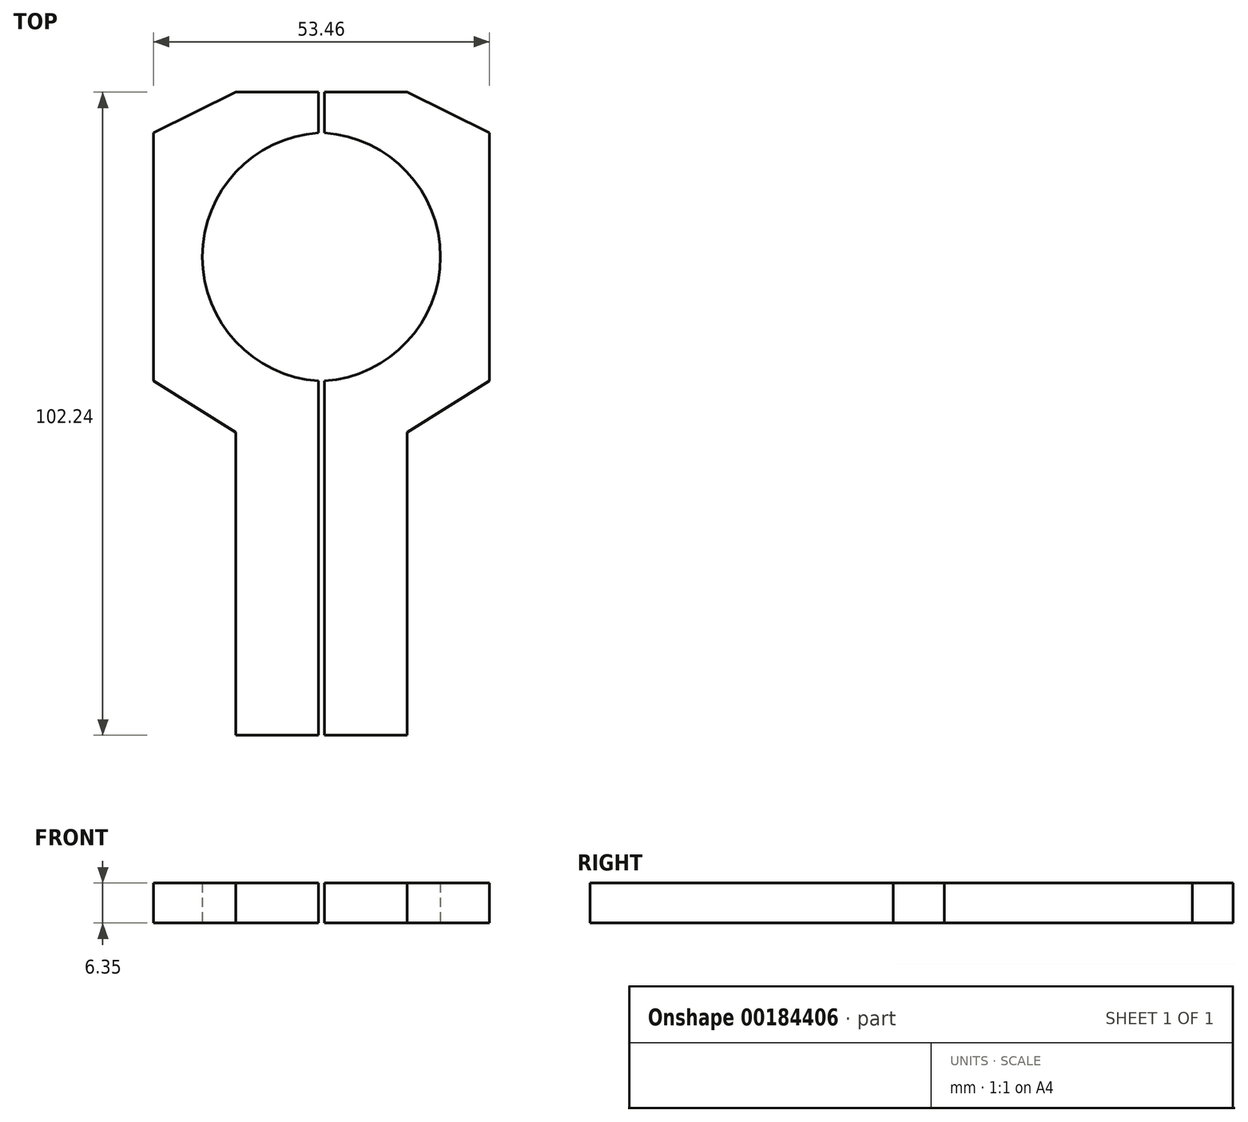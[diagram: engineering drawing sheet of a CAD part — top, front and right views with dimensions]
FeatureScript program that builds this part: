
annotation { "Feature Type Name" : "Feature", "Feature Type Description" : "" }
export const myFeature = defineFeature(function(context is Context, id is Id, definition is map)
    precondition{}
    {
        {
            var Q0;
            Q0=qCreatedBy(makeId("Top.planeOp"),FACE);
            var sketch = newSketch(context, id + "F0", { "sketchPlane" : qUnion([Q0])});
            skLineSegment(sketch, "E0.bottom", {"start": v(-0.47, 0) * mm, "end": v(-13.6, 0) * mm});
            skLineSegment(sketch, "E0.top", {"start": v(-0.47, -48.17) * mm, "end": v(-13.6, -48.17) * mm});
            skLineSegment(sketch, "E0.left", {"start": v(-0.47, 0) * mm, "end": v(-0.47, -48.17) * mm});
            skLineSegment(sketch, "E0.right", {"start": v(-13.6, 0) * mm, "end": v(-13.6, -48.17) * mm});
            skLineSegment(sketch, "E1", {"start": v(-13.6, 0) * mm, "end": v(-26.73, 8.15) * mm});
            skLineSegment(sketch, "E2", {"start": v(-26.73, 8.15) * mm, "end": v(-26.73, 47.59) * mm});
            skLineSegment(sketch, "E3", {"start": v(-26.73, 47.59) * mm, "end": v(-13.6, 54.07) * mm});
            skLineSegment(sketch, "E4", {"start": v(-13.6, 54.07) * mm, "end": v(-0.47, 54.07) * mm});
            skLineSegment(sketch, "E5", {"start": v(-0.47, 54.07) * mm, "end": v(-0.47, 47.59) * mm});
            skLineSegment(sketch, "E6", {"start": v(-0.47, 0) * mm, "end": v(-0.47, 8.15) * mm});
            skArc(sketch, "E7", {"start": v(-0.47, 47.59) * mm, "mid": v(-18.92, 27.87) * mm, "end": v(-0.47, 8.15) * mm});
            skPoint(sketch, "E7.third.point", {"position": v(-0.47, 8.15) * mm});
            skLineSegment(sketch, "E8.bottom", {"start": v(0.47, -48.17) * mm, "end": v(13.6, -48.17) * mm});
            skLineSegment(sketch, "E8.top", {"start": v(0.47, 0) * mm, "end": v(13.6, 0) * mm});
            skLineSegment(sketch, "E8.left", {"start": v(0.47, -48.17) * mm, "end": v(0.47, 0) * mm});
            skLineSegment(sketch, "E8.right", {"start": v(13.6, -48.17) * mm, "end": v(13.6, 0) * mm});
            skLineSegment(sketch, "E9", {"start": v(0.47, 0) * mm, "end": v(0.47, 8.15) * mm});
            skLineSegment(sketch, "E10", {"start": v(13.6, 0) * mm, "end": v(26.73, 8.15) * mm});
            skLineSegment(sketch, "E11", {"start": v(26.73, 8.15) * mm, "end": v(26.73, 47.59) * mm});
            skLineSegment(sketch, "E12", {"start": v(26.73, 47.59) * mm, "end": v(13.6, 54.07) * mm});
            skLineSegment(sketch, "E13", {"start": v(13.6, 54.07) * mm, "end": v(0.47, 54.07) * mm});
            skLineSegment(sketch, "E14", {"start": v(0.47, 54.07) * mm, "end": v(0.47, 47.59) * mm});
            skArc(sketch, "E15", {"start": v(0.47, 8.15) * mm, "mid": v(18.92, 27.87) * mm, "end": v(0.47, 47.59) * mm});
            skSolve(sketch);
        }
        {
            var Q0;
            Q0=makeQuery(id+"F0.imprint","IMPRINT",FACE,{"disambiguationData":[TD([[makeQuery(id+"F0.imprint","IMPRINT",EDGE,{"derivedFrom":sQuery(id+"F0.wireOp",EDGE,"E0.bottom")}),-1.0]])]});
            var Q1;
            Q1=makeQuery(id+"F0.imprint","IMPRINT",FACE,{"disambiguationData":[TD([[makeQuery(id+"F0.imprint","IMPRINT",EDGE,{"derivedFrom":sQuery(id+"F0.wireOp",EDGE,"E8.top")}),1.0]])]});
            var Q2;
            Q2=makeQuery(id+"F0.imprint","IMPRINT",FACE,{"disambiguationData":[TD([[makeQuery(id+"F0.imprint","IMPRINT",EDGE,{"derivedFrom":sQuery(id+"F0.wireOp",EDGE,"E8.bottom")}),1.0]])]});
            var Q3;
            Q3=makeQuery(id+"F0.imprint","IMPRINT",FACE,{"disambiguationData":[TD([[makeQuery(id+"F0.imprint","IMPRINT",EDGE,{"derivedFrom":sQuery(id+"F0.wireOp",EDGE,"E0.bottom")}),1.0]])]});
            extrude(context, id + "F1", {"entities" : qUnion([Q0, Q1, Q2, Q3]), "depth" : 6.35 * mm});
        }
    });
